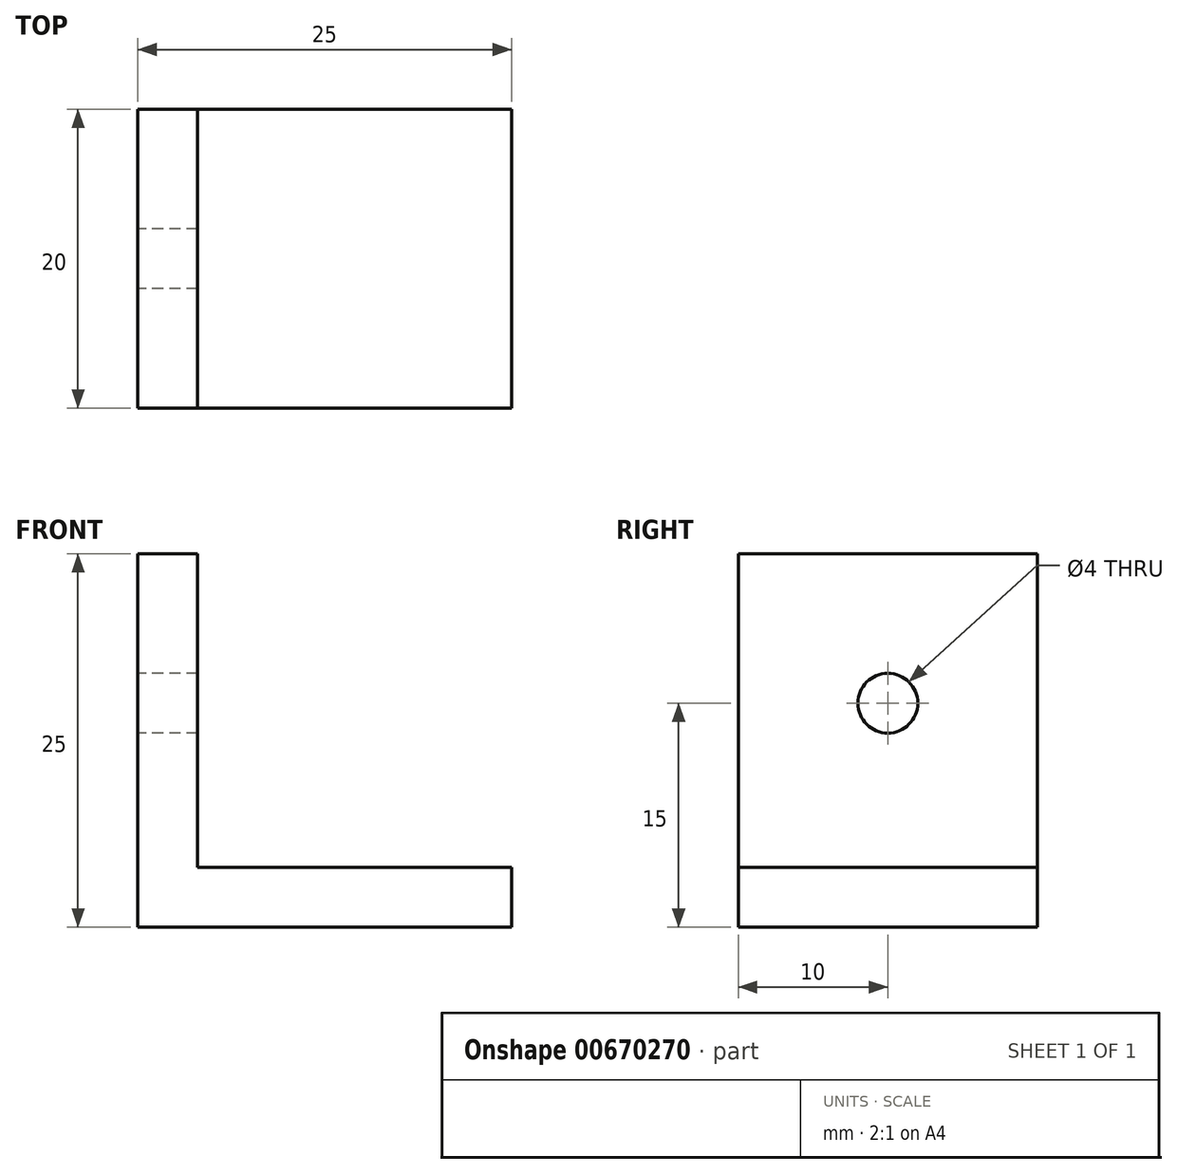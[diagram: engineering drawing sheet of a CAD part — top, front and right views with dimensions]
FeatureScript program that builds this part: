
annotation { "Feature Type Name" : "Feature", "Feature Type Description" : "" }
export const myFeature = defineFeature(function(context is Context, id is Id, definition is map)
    precondition{}
    {
        {
            var Q0;
            Q0=qCreatedBy(makeId("Front.planeOp"),FACE);
            var sketch = newSketch(context, id + "F0", { "sketchPlane" : qUnion([Q0])});
            skLineSegment(sketch, "E0", {"start": v(0, 0) * mm, "end": v(-25, 0) * mm});
            skLineSegment(sketch, "E1", {"start": v(-25, 0) * mm, "end": v(-25, 25) * mm});
            skLineSegment(sketch, "E2", {"start": v(-25, 25) * mm, "end": v(-21, 25) * mm});
            skLineSegment(sketch, "E3", {"start": v(-21, 25) * mm, "end": v(-21, 4) * mm});
            skLineSegment(sketch, "E4", {"start": v(-21, 4) * mm, "end": v(0, 4) * mm});
            skLineSegment(sketch, "E5", {"start": v(0, 4) * mm, "end": v(0, 0) * mm});
            skSolve(sketch);
        }
        {
            var Q0;
            Q0=makeQuery(id+"F0.imprint","IMPRINT",FACE,{"disambiguationData":[TD([[makeQuery(id+"F0.imprint","IMPRINT",EDGE,{"derivedFrom":sQuery(id+"F0.wireOp",EDGE,"E0")}),-1.0]])]});
            extrude(context, id + "F1", {"entities" : qUnion([Q0]), "depth" : 20 * mm, "offsetDistance" : 25 * mm});
        }
        {
            var Q0;
            Q0=makeQuery(id+"F1.opExtrude","SWEPT_FACE",FACE,{"disambiguationData":[OSD([sQuery(id+"F0.wireOp",EDGE,"E1")])]});
            var sketch = newSketch(context, id + "F2", { "sketchPlane" : qUnion([Q0])});
            skCircle(sketch, "E6", {"center": v(10, 15) * mm, "radius": 2 * mm});
            skSolve(sketch);
        }
        {
            var Q0;
            Q0=sQuery(id+"F2.wireOp",VERTEX,"E6.center");
            var Q1;
            Q1=makeQuery(id+"F1.opExtrude","SWEPT_BODY",BODY,{"disambiguationData":[OSD([sQuery(id+"F0.wireOp",EDGE,"E0"),sQuery(id+"F0.wireOp",EDGE,"E1"),sQuery(id+"F0.wireOp",EDGE,"E2"),sQuery(id+"F0.wireOp",EDGE,"E3"),sQuery(id+"F0.wireOp",EDGE,"E4"),sQuery(id+"F0.wireOp",EDGE,"E5")])]});
            hole(context, id + "F3", {"style" : HoleStyle.SIMPLE, "endStyle" : HoleEndStyle.THROUGH, "holeDiameter" : 4 * mm, "majorDiameter" : 5 * mm, "isTappedThrough" : true, "tappedDepth" : 12 * mm, "tapClearance" : 3, "locations" : qUnion([Q0]), "scope" : qUnion([Q1])});
        }
    });
